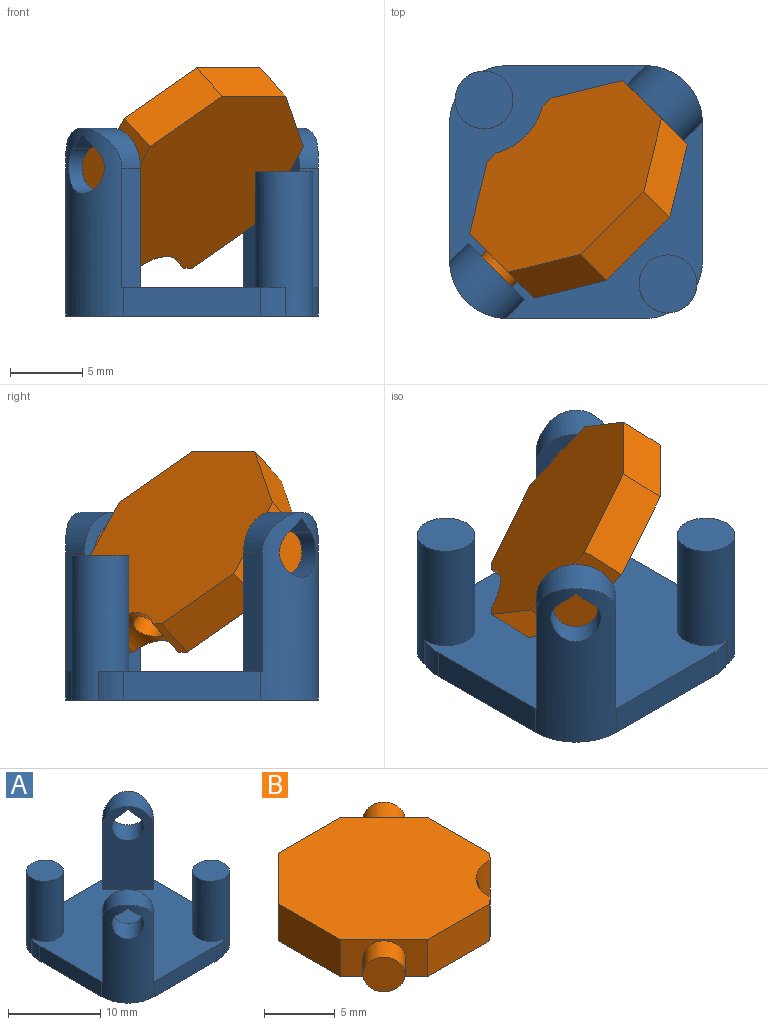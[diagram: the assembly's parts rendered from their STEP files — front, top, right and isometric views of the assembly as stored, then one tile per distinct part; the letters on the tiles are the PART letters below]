
ASSEMBLY  parts=2 mates=1
PART A: 38 faces, bbox 19.1x19.1x13 mm
  f0: plane 17.5x17.5mm, normal (0,0,1), area 240.1mm2, adj f1,f2,f3,f4,f5,f6,f7,f8
  f1: plane 9.5x2mm, normal (1,0,0), area 19mm2, adj f0,f2,f12,f13
  f2: cylinder r=4mm len=13mm, axis (0,0,1), area 65mm2, adj f0,f1,f3,f13,f16,f17,f19,f20
  f3: plane 9.5x2mm, normal (0,1,0), area 19mm2, adj f0,f2,f4,f13
  f4: cylinder r=4mm len=2mm, axis (0,0,1), area 3.6mm2, adj f0,f3,f5,f13
  f5: cylinder r=2mm len=10mm, axis (0,0,1), area 106.4mm2, adj f0,f4,f6,f13,f31
  f6: cylinder r=4mm len=2mm, axis (0,0,1), area 3.6mm2, adj f0,f5,f7,f13
  f7: plane 9.5x2mm, normal (-1,0,0), area 19mm2, adj f0,f6,f8,f13
  f8: cylinder r=4mm len=13mm, axis (0,0,1), area 65mm2, adj f0,f7,f9,f13,f24,f25,f26,f27
  f9: plane 9.5x2mm, normal (0,-1,0), area 19mm2, adj f0,f8,f10,f13
  f10: cylinder r=4mm len=2mm, axis (0,0,1), area 3.6mm2, adj f0,f9,f11,f13
  f11: cylinder r=2mm len=10mm, axis (0,0,1), area 106.4mm2, adj f0,f10,f12,f13,f33
  f12: cylinder r=4mm len=2mm, axis (0,0,1), area 3.6mm2, adj f0,f1,f11,f13
  f13: plane 17.5x17.5mm, normal (0,0,-1), area 272.2mm2, adj f1,f2,f3,f4,f5,f6,f7,f8
  f14: cylinder r=1.4mm len=8mm, axis (0,0,-1), area 70.4mm2, adj f13,f30
  f15: cylinder r=1.4mm len=8mm, axis (0,0,-1), area 70.4mm2, adj f13,f32
  f16: plane 8.25x1.29mm, normal (0.71,-0.71,0), area 15mm2, adj f0,f2,f18,f22
  f17: plane 8.25x1.29mm, normal (-0.71,0.71,0), area 15mm2, adj f0,f2,f18,f22
  f18: plane 11x3.89mm, normal (-0.71,-0.71,0), area 47.2mm2, adj f0,f16,f17,f19,f20,f21,f22
  f19: cylinder r=1.75mm len=4.54mm, axis (-0.71,-0.71,0), area 22.8mm2, adj f2,f18,f20,f21
  f20: plane 2.88x2.77mm, normal (-0.46,0.46,-0.76), area 4.3mm2, adj f2,f18,f19,f21
  f21: plane 2.88x2.77mm, normal (0.46,-0.46,-0.76), area 4.3mm2, adj f2,f18,f19,f20
  f22: cylinder r=2.75mm len=5.95mm, axis (-0.71,-0.71,0), area 20.7mm2, adj f2,f16,f17,f18
  f23: plane 11x3.89mm, normal (0.71,0.71,0), area 47.2mm2, adj f0,f24,f25,f26,f27,f28,f29
  f24: plane 8.25x1.29mm, normal (0.71,-0.71,0), area 15mm2, adj f0,f8,f23,f29
  f25: plane 8.25x1.29mm, normal (-0.71,0.71,0), area 15mm2, adj f0,f8,f23,f29
  f26: cylinder r=1.75mm len=4.54mm, axis (0.71,0.71,0), area 22.8mm2, adj f8,f23,f27,f28
  f27: plane 2.88x2.77mm, normal (0.46,-0.46,-0.76), area 4.3mm2, adj f8,f23,f26,f28
  f28: plane 2.88x2.77mm, normal (-0.46,0.46,-0.76), area 4.3mm2, adj f8,f23,f26,f27
  f29: cylinder r=2.75mm len=5.95mm, axis (-0.71,-0.71,0), area 20.7mm2, adj f8,f23,f24,f25
  f30: cone r=0mm half-angle=59deg, axis (0,0,-1), area 7.2mm2, adj f14
  f31: plane 4x4mm, normal (0,0,1), area 12.6mm2, adj f5
  f32: cone r=0mm half-angle=59deg, axis (0,0,-1), area 7.2mm2, adj f15
  f33: plane 4x4mm, normal (0,0,1), area 12.6mm2, adj f11
  f34: cone r=0mm half-angle=59deg, axis (0,0,-1), area 5.3mm2, adj f35
  f35: cylinder r=1.2mm len=2.4mm, axis (0,0,-1), area 11.3mm2, adj f13,f34
  f36: cone r=0mm half-angle=59deg, axis (0,0,-1), area 5.3mm2, adj f37
  f37: cylinder r=1.2mm len=2.4mm, axis (0,0,-1), area 11.3mm2, adj f13,f36
PART B: 18 faces, bbox 15.6x15.6x3.2 mm
  f0: plane 3.2x0.62mm, normal (0.71,-0.71,0), area 2.8mm2, adj f1,f9,f10,f11
  f1: plane 6.21x3.2mm, normal (1,0,0), area 19.9mm2, adj f0,f2,f9,f10
  f2: plane 4.39x4.39mm, normal (0.71,0.71,0), area 12.8mm2, adj f1,f3,f9,f10,f14
  f3: plane 6.21x3.2mm, normal (0,1,0), area 19.9mm2, adj f2,f4,f9,f10
  f4: plane 4.39x4.39mm, normal (-0.71,0.71,0), area 19.9mm2, adj f3,f5,f9,f10
  f5: plane 6.21x3.2mm, normal (-1,0,0), area 19.9mm2, adj f4,f6,f9,f10
  f6: plane 4.39x4.39mm, normal (-0.71,-0.71,0), area 12.8mm2, adj f5,f7,f9,f10,f16
  f7: plane 6.21x3.2mm, normal (0,-1,0), area 19.9mm2, adj f6,f8,f9,f10
  f8: plane 3.2x0.62mm, normal (0.71,-0.71,0), area 2.8mm2, adj f7,f9,f10,f11
  f9: plane 15x15mm, normal (0,0,1), area 183.3mm2, adj f0,f1,f2,f3,f4,f5,f6,f7
  f10: plane 15x15mm, normal (0,0,-1), area 183.3mm2, adj f0,f1,f2,f3,f4,f5,f6,f7
  f11: cylinder r=3mm len=3.2mm, axis (0,0,1), area 11.9mm2, adj f0,f8,f9,f10,f13
  f12: plane 2.3x1.63mm, normal (0.71,-0.71,0), area 4.2mm2, adj f13
  f13: cylinder r=1.15mm len=9.92mm, axis (0.71,-0.71,0), area 83.9mm2, adj f11,f12
  f14: cylinder r=1.5mm len=3.54mm, axis (-0.71,-0.71,0), area 18.8mm2, adj f2,f15
  f15: plane 3x2.12mm, normal (0.71,0.71,0), area 7.1mm2, adj f14
  f16: cylinder r=1.5mm len=3.54mm, axis (0.71,0.71,0), area 18.8mm2, adj f6,f17
  f17: plane 3x2.12mm, normal (-0.71,-0.71,0), area 7.1mm2, adj f16
PLACE A t=(9.46,5.43,-4.65)mm fixed
PLACE B rot(axis=(0.71,0.71,0),127.4deg) t=(8.74,6.5,4.57)mm
MATE cylindrical A.f26 <-> B.f14  axis (-0.71,-0.71,0) through (14.98,10.95,3.6)mm
